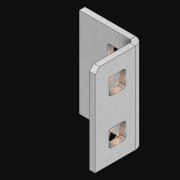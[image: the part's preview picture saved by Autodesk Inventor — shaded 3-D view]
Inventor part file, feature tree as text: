
AUTODESK INVENTOR PART (.ipt)
format: ipt  version: 2021 (Build 250183000, 183)  size: 1,021,440 bytes
history: native  units: in
note: dims shown in document units (in); Inventor stores cm internally (conversion verified against a paired STEP export)
features: extrude x6, sketch x4, other x4, pattern_linear x2, sheet_metal_op x1
ambient origin geometry x8: Origin, YZ Plane, XZ Plane, XY Plane, X Axis, Y Axis, Z Axis, Center Point
bodies: Solid1 (feature_tree)
feature tree (17):
  pattern_linear  "Rectangular Pattern1"  Spacing1=0.5in  [1 undecoded]
  pattern_linear  "Rectangular Pattern3"  Count1=2  [1 undecoded]
  extrude  "Extrusion1"  Depth=0.5in
  extrude  "Extrusion2"  Depth=0.841in
  sketch  "Sketch1"  dims[d0=0.182in]
  other  "Srf1"
  sketch  "Sketch3"  dims[d1=0.063in d2=0.0in]
  other  "Srf3"
  other  "Srf4"
  other  "Srf142"
  sketch  "Sketch4"  dims[d6=0.182in]
  sketch  "Sketch5"  dims[d7=0.063in d8=0.0in d11=0.5in d12=0.3937in d14=0.5in d18=0.7874in d20=0.5in d21=16.5in d22=0.0in d23=0.841in d24=0.0in]
  sheet_metal_op  "Fold1"
  extrude  "ExtrusionSrf1"  TaperAngle=0.0deg  [1 undecoded]
  extrude  "ExtrusionSrf3"  Depth=0.841in TaperAngle=0.0deg
  extrude  "ExtrusionSrf4"  [1 undecoded]
  extrude  "ExtrusionSrf142"  [1 undecoded]
note: 5 required parameter values undecoded (feature->parameter linkage not recoverable at this tier; creation-order binding heuristic only, values carry confidence <= 0.55)
